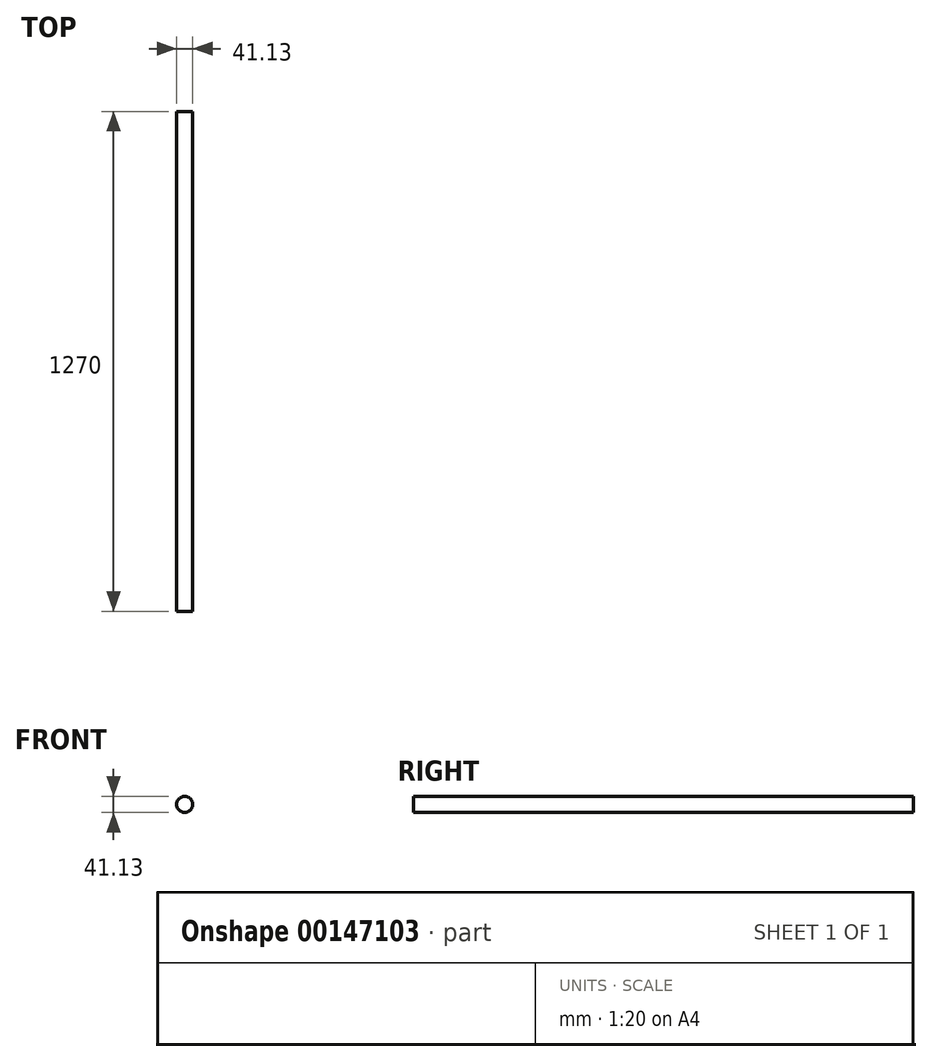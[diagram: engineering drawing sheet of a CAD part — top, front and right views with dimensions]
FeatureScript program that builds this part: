
annotation { "Feature Type Name" : "Feature", "Feature Type Description" : "" }
export const myFeature = defineFeature(function(context is Context, id is Id, definition is map)
    precondition{}
    {
        {
            var Q0;
            Q0=qCreatedBy(makeId("Front.planeOp"),FACE);
            var sketch = newSketch(context, id + "F0", { "sketchPlane" : qUnion([Q0])});
            skCircle(sketch, "E0", {"center": v(-34.95, 16.25) * mm, "radius": 20.56 * mm});
            skSolve(sketch);
        }
        {
            var Q0;
            Q0=makeQuery(id+"F0.imprint","IMPRINT",FACE,{"disambiguationData":[TD([[makeQuery(id+"F0.imprint","IMPRINT",EDGE,{"derivedFrom":sQuery(id+"F0.wireOp",EDGE,"E0")}),1.0]])]});
            extrude(context, id + "F1", {"entities" : qUnion([Q0]), "depth" : 1270 * mm});
        }
    });
